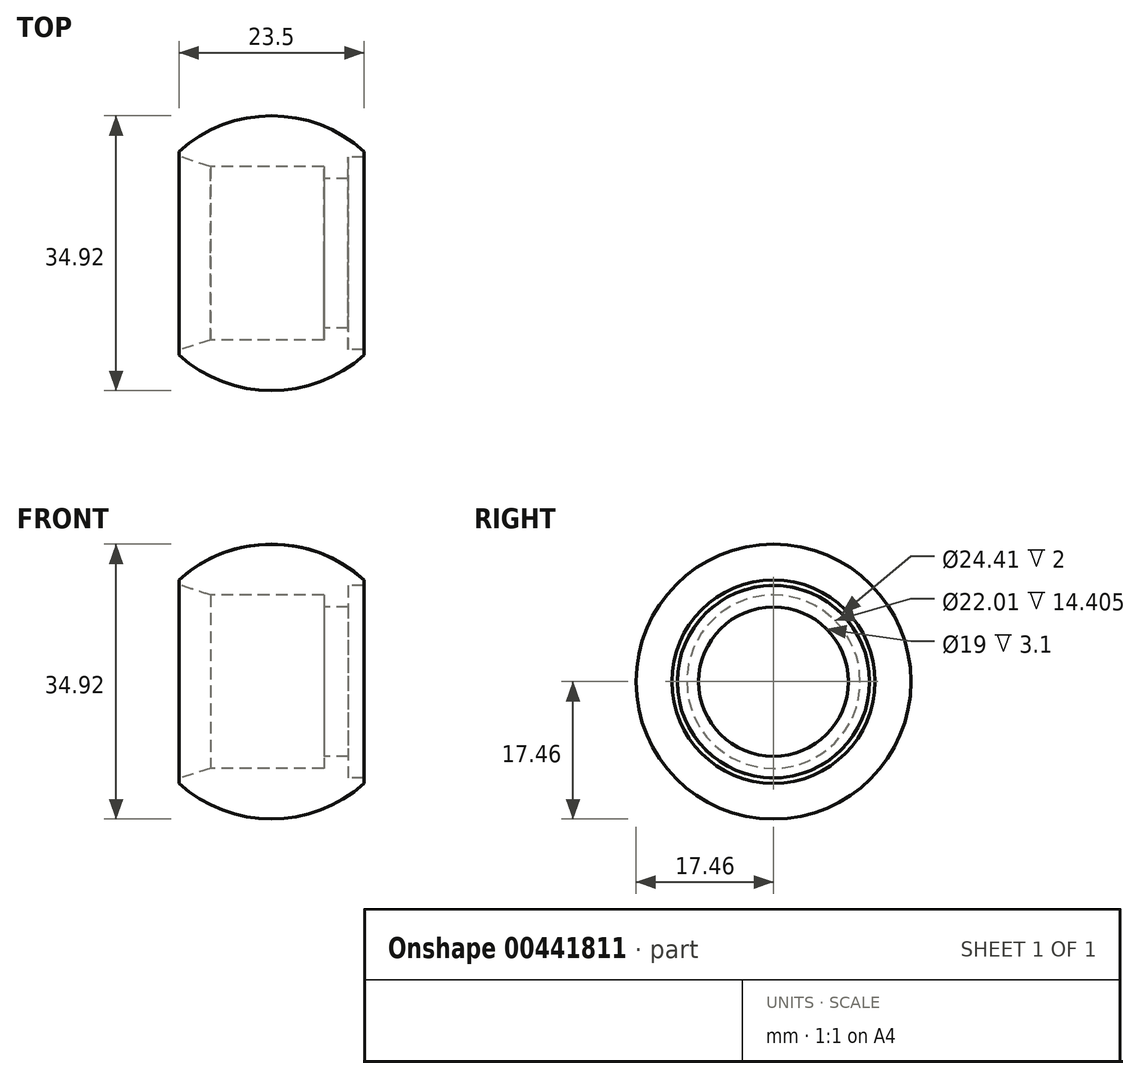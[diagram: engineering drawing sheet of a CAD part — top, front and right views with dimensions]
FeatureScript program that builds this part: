
annotation { "Feature Type Name" : "Feature", "Feature Type Description" : "" }
export const myFeature = defineFeature(function(context is Context, id is Id, definition is map)
    precondition{}
    {
        {
            var Q0;
            Q0=qCreatedBy(makeId("Front.planeOp"),FACE);
            var sketch = newSketch(context, id + "F0", { "sketchPlane" : qUnion([Q0])});
            skLineSegment(sketch, "E0", {"start": v(-16.25, 0) * mm, "end": v(16.25, 0) * mm, "construction": true});
            skLineSegment(sketch, "E1", {"start": v(11.75, 12.2) * mm, "end": v(11.75, 12.91) * mm});
            skArc(sketch, "E2", {"start": v(11.75, 12.91) * mm, "mid": v(0, 17.46) * mm, "end": v(-11.75, 12.91) * mm});
            skLineSegment(sketch, "E3", {"start": v(-11.75, 12.91) * mm, "end": v(11.75, 12.91) * mm, "construction": true});
            skLineSegment(sketch, "E4", {"start": v(11.75, 12.2) * mm, "end": v(11.75, 0) * mm, "construction": true});
            skLineSegment(sketch, "E5", {"start": v(11.75, 12.2) * mm, "end": v(9.75, 12.2) * mm});
            skLineSegment(sketch, "E6", {"start": v(9.75, 12.2) * mm, "end": v(9.75, 9.5) * mm});
            skLineSegment(sketch, "E7", {"start": v(9.75, 9.5) * mm, "end": v(9.75, 0) * mm, "construction": true});
            skLineSegment(sketch, "E8", {"start": v(9.75, 9.5) * mm, "end": v(6.65, 9.5) * mm});
            skLineSegment(sketch, "E9", {"start": v(6.65, 11) * mm, "end": v(6.65, 9.5) * mm});
            skLineSegment(sketch, "E10", {"start": v(-11.75, 12.91) * mm, "end": v(-11.75, 12.31) * mm});
            skLineSegment(sketch, "E11", {"start": v(-7.76, 11) * mm, "end": v(-11.75, 12.31) * mm});
            skLineSegment(sketch, "E12", {"start": v(-7.76, 11) * mm, "end": v(6.65, 11) * mm});
            skSolve(sketch);
        }
        {
            var Q0;
            Q0=makeQuery(id+"F0.imprint","IMPRINT",FACE,{"disambiguationData":[TD([[makeQuery(id+"F0.imprint","IMPRINT",EDGE,{"derivedFrom":sQuery(id+"F0.wireOp",EDGE,"E1")}),1.0]])]});
            var Q1;
            Q1=sQuery(id+"F0.wireOp",EDGE,"E0");
            revolve(context, id + "F1", {"entities" : qUnion([Q0]), "axis" : qUnion([Q1]), "revolveType" : RevolveType.FULL});
        }
    });
